# Revit family: RRHPLT
name_source: partatom
category: Generic Models
revit_build: Autodesk Revit 2018 (Build: 20190510_1515(x64)
units: mm (PartAtom-declared; Revit-internal decimal feet)

## family parameters
Always vertical = No
Can host rebar = No
Cut with Voids When Loaded = No
Part Type = Normal
Room Calculation Point = No
Round Connector Dimension = Use Diameter
Shared = Yes
Work Plane-Based = Yes

## types (3) — shared parameters
Default Elevation = 48 "
Gasket Material = <By Category>
Length = 4 "
Outer Radius = 0.25 "
Plate Material = <By Category>
Width = 1.5 "

## per-type parameters (varying)
| type | Description | Rod Type | Standoff Rod |
| RRHPLT02 | Rocket Plate Hygienic 304 1/4 Inch X 1-1/2 Inch X 4 Inch w/FDA Compliant Silicone Gasket w/2 Inch Extension from Wall | RMRRHPLTBROD : RMRRHPLT02BROD | Yes |
| RRHPLT | Rocket Plate Hygienic 304 1/4 Inch X 1-1/2 Inch X 4 Inch w/FDA Compliant Silicone Gasket w/No Extension | RMRRHPLTBROD : RMRRHPLT02BROD | No |
| RRHPLT04 | Rocket Plate Hygienic 304 1/4 Inch X 1-1/2 Inch X 4 Inch w/FDA Compliant Silicone Gasket w/4 Inch Extension from Wall | RMRRHPLTBROD : RMRRHPLT04BROD | Yes |

note: column(s) folded — value = type name in every type: Catalog Number

## geometry (parser evidence)
native form markers: Sweep x11
no freeform markers — native parametric forms only
